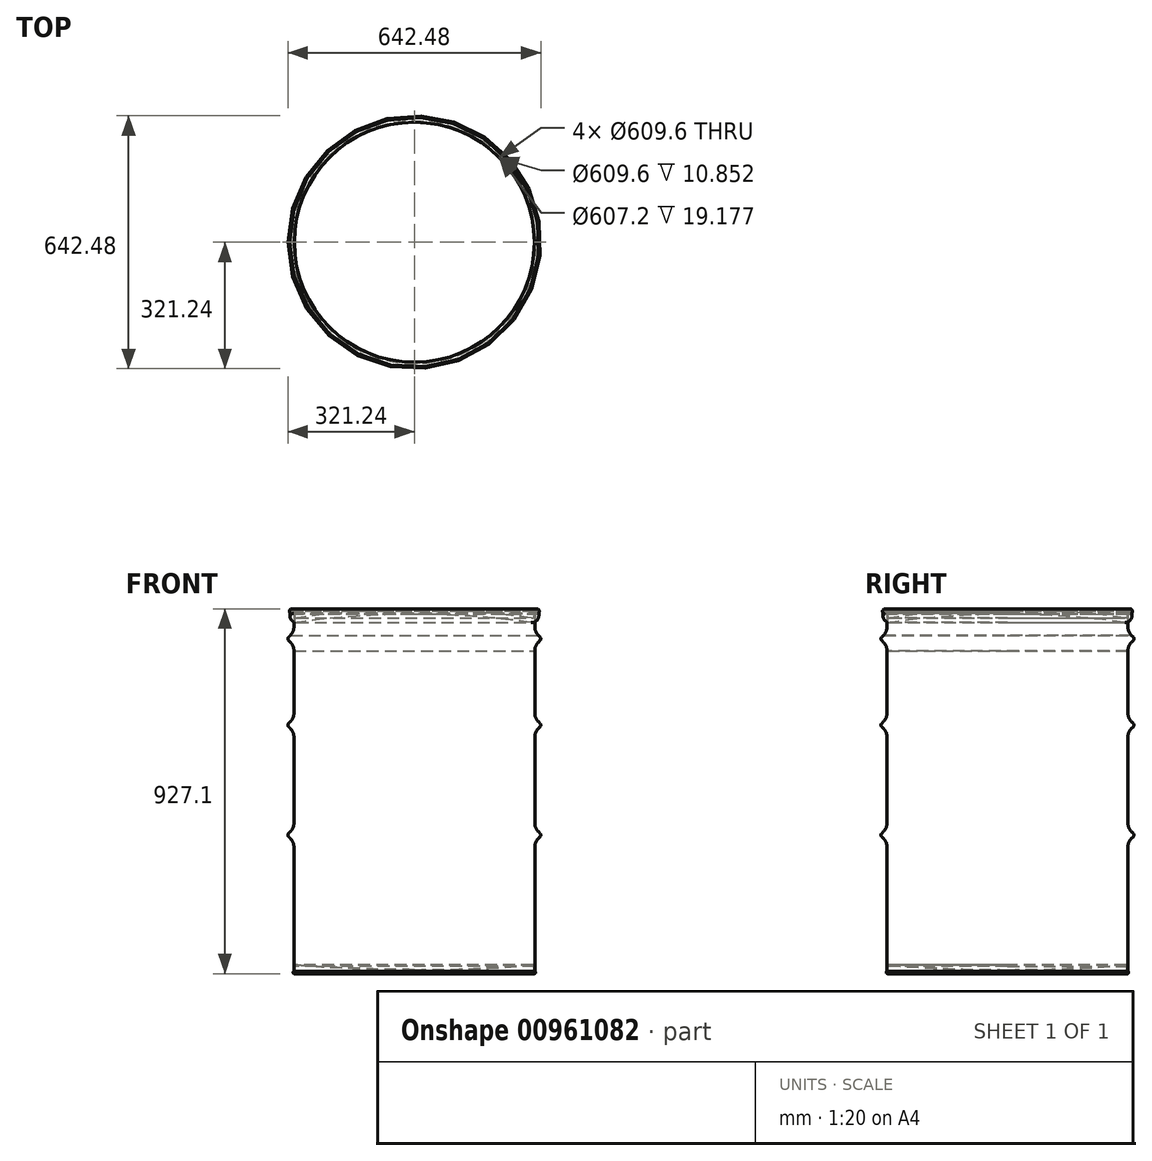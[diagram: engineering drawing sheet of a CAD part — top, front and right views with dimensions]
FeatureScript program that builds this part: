
annotation { "Feature Type Name" : "Feature", "Feature Type Description" : "" }
export const myFeature = defineFeature(function(context is Context, id is Id, definition is map)
    precondition{}
    {
        {
            var Q0;
            Q0=qCreatedBy(makeId("Front.planeOp"),FACE);
            var sketch = newSketch(context, id + "F0", { "sketchPlane" : qUnion([Q0])});
            skLineSegment(sketch, "E0.top", {"start": v(-306, 920.75) * mm, "end": v(-304.8, 920.75) * mm, "construction": true});
            skLineSegment(sketch, "E0.right", {"start": v(-304.8, 0) * mm, "end": v(-304.8, 321.86) * mm});
            skLineSegment(sketch, "E1", {"start": v(0, 0) * mm, "end": v(0, 177.34) * mm, "construction": true});
            skArc(sketch, "E2", {"start": v(-304.8, 920.75) * mm, "mid": v(-316.84, 923.57) * mm, "end": v(-307.3, 915.7) * mm});
            skArc(sketch, "E3", {"start": v(-306, 920.75) * mm, "mid": v(-315.77, 923.04) * mm, "end": v(-308.03, 916.65) * mm});
            skLineSegment(sketch, "E4", {"start": v(-308.03, 916.65) * mm, "end": v(-307.3, 915.7) * mm});
            skArc(sketch, "E5", {"start": v(-304.8, 0) * mm, "mid": v(-307.92, 2.56) * mm, "end": v(-306, 6.11) * mm});
            skLineSegment(sketch, "E6.trimOffspring", {"start": v(-306, 6.11) * mm, "end": v(-306, 321.86) * mm});
            skPoint(sketch, "E0.left.start.orphan", {"position": v(-306, 0) * mm});
            skLineSegment(sketch, "E7", {"start": v(-314.89, 859.88) * mm, "end": v(-319.38, 855.4) * mm});
            skLineSegment(sketch, "E8", {"start": v(-319.38, 846.4) * mm, "end": v(-314.89, 841.92) * mm});
            skLineSegment(sketch, "E9.trimOffspring", {"start": v(-306, 881.34) * mm, "end": v(-306, 920.75) * mm});
            skArc(sketch, "E10.filletArc", {"start": v(-319.38, 855.4) * mm, "mid": v(-321.24, 850.9) * mm, "end": v(-319.38, 846.4) * mm});
            skArc(sketch, "E11.filletArc", {"start": v(-314.89, 859.88) * mm, "mid": v(-308.31, 869.73) * mm, "end": v(-306, 881.34) * mm});
            skArc(sketch, "E12.filletArc", {"start": v(-306, 820.46) * mm, "mid": v(-308.31, 832.07) * mm, "end": v(-314.89, 841.92) * mm});
            skLineSegment(sketch, "E13", {"start": v(-321.24, 805.66) * mm, "end": v(-321.24, 227.24) * mm, "construction": true});
            skLineSegment(sketch, "E14", {"start": v(-311.15, 920.75) * mm, "end": v(-311.15, 927.1) * mm, "construction": true});
            skLineSegment(sketch, "E15", {"start": v(-319.38, 855.4) * mm, "end": v(-319.38, 846.4) * mm, "construction": true});
            skLineSegment(sketch, "E16", {"start": v(-314.89, 859.88) * mm, "end": v(-314.89, 841.92) * mm, "construction": true});
            skLineSegment(sketch, "E17", {"start": v(-306, 820.46) * mm, "end": v(-304.8, 820.46) * mm, "construction": true});
            skLineSegment(sketch, "E18", {"start": v(-306, 881.34) * mm, "end": v(-304.8, 881.34) * mm, "construction": true});
            skLineSegment(sketch, "E19.trimOffspring", {"start": v(-304.8, 881.34) * mm, "end": v(-304.8, 920.75) * mm});
            skLineSegment(sketch, "E20", {"start": v(-318.4, 847.39) * mm, "end": v(-313.91, 842.9) * mm});
            skLineSegment(sketch, "E21", {"start": v(-318.4, 854.41) * mm, "end": v(-313.91, 858.9) * mm});
            skArc(sketch, "E22", {"start": v(-318.4, 854.41) * mm, "mid": v(-319.86, 850.9) * mm, "end": v(-318.4, 847.39) * mm});
            skArc(sketch, "E23", {"start": v(-313.91, 858.9) * mm, "mid": v(-307.17, 869.23) * mm, "end": v(-304.8, 881.34) * mm});
            skArc(sketch, "E24", {"start": v(-304.8, 820.46) * mm, "mid": v(-307.08, 832.6) * mm, "end": v(-313.91, 842.9) * mm});
            skLineSegment(sketch, "E25", {"start": v(-314.89, 640.68) * mm, "end": v(-319.38, 636.19) * mm});
            skLineSegment(sketch, "E26", {"start": v(-319.38, 627.2) * mm, "end": v(-314.89, 622.72) * mm});
            skLineSegment(sketch, "E27.trimOffspring", {"start": v(-306, 662.14) * mm, "end": v(-306, 820.46) * mm});
            skPoint(sketch, "E28.visualSharp", {"position": v(-323.87, 631.7) * mm});
            skArc(sketch, "E28.filletArc", {"start": v(-319.38, 636.19) * mm, "mid": v(-321.24, 631.7) * mm, "end": v(-319.38, 627.2) * mm});
            skArc(sketch, "E29.filletArc", {"start": v(-314.89, 640.68) * mm, "mid": v(-308.31, 650.53) * mm, "end": v(-306, 662.14) * mm});
            skArc(sketch, "E30.filletArc", {"start": v(-306, 601.26) * mm, "mid": v(-308.31, 612.87) * mm, "end": v(-314.89, 622.72) * mm});
            skLineSegment(sketch, "E31", {"start": v(-314.89, 640.68) * mm, "end": v(-314.89, 622.72) * mm, "construction": true});
            skLineSegment(sketch, "E32", {"start": v(-306, 601.26) * mm, "end": v(-304.8, 601.26) * mm, "construction": true});
            skLineSegment(sketch, "E33", {"start": v(-306, 662.14) * mm, "end": v(-304.8, 662.14) * mm, "construction": true});
            skLineSegment(sketch, "E34.trimOffspring", {"start": v(-304.8, 662.14) * mm, "end": v(-304.8, 820.46) * mm});
            skLineSegment(sketch, "E35", {"start": v(-318.53, 635.34) * mm, "end": v(-314.04, 639.83) * mm});
            skArc(sketch, "E36", {"start": v(-314.04, 639.83) * mm, "mid": v(-307.2, 650.07) * mm, "end": v(-304.8, 662.14) * mm});
            skLineSegment(sketch, "E37", {"start": v(-318.53, 628.06) * mm, "end": v(-314.04, 623.57) * mm});
            skArc(sketch, "E38", {"start": v(-304.8, 601.26) * mm, "mid": v(-307.2, 613.33) * mm, "end": v(-314.04, 623.57) * mm});
            skArc(sketch, "E39", {"start": v(-318.53, 635.34) * mm, "mid": v(-320.04, 631.7) * mm, "end": v(-318.53, 628.06) * mm});
            skLineSegment(sketch, "E40", {"start": v(-314.89, 361.28) * mm, "end": v(-319.38, 356.79) * mm});
            skLineSegment(sketch, "E41", {"start": v(-319.38, 347.8) * mm, "end": v(-314.9, 343.32) * mm});
            skArc(sketch, "E42.filletArc", {"start": v(-319.38, 356.79) * mm, "mid": v(-321.24, 352.3) * mm, "end": v(-319.38, 347.8) * mm});
            skLineSegment(sketch, "E43.trimOffspring", {"start": v(-306, 382.74) * mm, "end": v(-306, 601.26) * mm});
            skArc(sketch, "E44.filletArc", {"start": v(-314.9, 361.28) * mm, "mid": v(-308.31, 371.13) * mm, "end": v(-306, 382.74) * mm});
            skArc(sketch, "E45.filletArc", {"start": v(-306, 321.86) * mm, "mid": v(-308.31, 333.47) * mm, "end": v(-314.89, 343.32) * mm});
            skLineSegment(sketch, "E46", {"start": v(-319.38, 356.79) * mm, "end": v(-319.38, 347.8) * mm, "construction": true});
            skLineSegment(sketch, "E47", {"start": v(-314.89, 361.28) * mm, "end": v(-314.89, 343.32) * mm, "construction": true});
            skLineSegment(sketch, "E48", {"start": v(-306, 382.74) * mm, "end": v(-304.8, 382.74) * mm, "construction": true});
            skLineSegment(sketch, "E49", {"start": v(-306, 321.86) * mm, "end": v(-304.8, 321.86) * mm, "construction": true});
            skLineSegment(sketch, "E50.trimOffspring", {"start": v(-304.8, 382.74) * mm, "end": v(-304.8, 601.26) * mm});
            skLineSegment(sketch, "E51", {"start": v(-318.53, 355.94) * mm, "end": v(-314.04, 360.43) * mm});
            skLineSegment(sketch, "E52", {"start": v(-318.53, 348.66) * mm, "end": v(-314.04, 344.17) * mm});
            skArc(sketch, "E53", {"start": v(-314.04, 360.43) * mm, "mid": v(-307.2, 370.67) * mm, "end": v(-304.8, 382.74) * mm});
            skArc(sketch, "E54", {"start": v(-304.8, 321.86) * mm, "mid": v(-307.2, 333.93) * mm, "end": v(-314.04, 344.17) * mm});
            skArc(sketch, "E55", {"start": v(-318.53, 355.94) * mm, "mid": v(-320.04, 352.3) * mm, "end": v(-318.53, 348.66) * mm});
            skSolve(sketch);
        }
        {
            var Q0;
            Q0=qSketchRegion(id+"F0",true);
            var Q1;
            Q1=qConstructionFilter(qBodyType(qCreatedBy(id+"F0",EDGE),BodyType.WIRE),ConstructionObject.NO);
            var Q2;
            Q2=sQuery(id+"F0.wireOp",EDGE,"E1");
            revolve(context, id + "F1", {"entities" : qUnion([Q0]), "surfaceEntities" : qUnion([Q1]), "axis" : qUnion([Q2]), "revolveType" : RevolveType.FULL});
        }
        {
            var Q0;
            Q0=qCreatedBy(makeId("Front.planeOp"),FACE);
            var sketch = newSketch(context, id + "F2", { "sketchPlane" : qUnion([Q0])});
            skLineSegment(sketch, "E56", {"start": v(306, 6.11) * mm, "end": v(306, 321.86) * mm});
            skArc(sketch, "E57", {"start": v(304.8, 0) * mm, "mid": v(307.92, 2.56) * mm, "end": v(306, 6.11) * mm});
            skLineSegment(sketch, "E58", {"start": v(304.8, 0) * mm, "end": v(304.8, 321.86) * mm});
            skLineSegment(sketch, "E59", {"start": v(-304.8, 321.86) * mm, "end": v(-304.8, 0) * mm});
            skLineSegment(sketch, "E60", {"start": v(-304.8, 0) * mm, "end": v(-303.6, 0) * mm});
            skLineSegment(sketch, "E61", {"start": v(-303.6, 0) * mm, "end": v(-303.6, 19.18) * mm});
            skArc(sketch, "E62", {"start": v(-301.47, 21.15) * mm, "mid": v(-302.96, 20.63) * mm, "end": v(-303.6, 19.18) * mm});
            skLineSegment(sketch, "E63", {"start": v(0, 244.83) * mm, "end": v(0, -50.53) * mm, "construction": true});
            skArc(sketch, "E64", {"start": v(-301.47, 21.15) * mm, "mid": v(-150.85, 12.15) * mm, "end": v(0, 9.14) * mm});
            skLineSegment(sketch, "E65", {"start": v(0, 9.14) * mm, "end": v(0, 10.34) * mm});
            skArc(sketch, "E66", {"start": v(-304.8, 19.18) * mm, "mid": v(-303.78, 21.5) * mm, "end": v(-301.37, 22.34) * mm});
            skArc(sketch, "E67", {"start": v(-301.37, 22.34) * mm, "mid": v(-150.8, 13.34) * mm, "end": v(0, 10.34) * mm});
            skLineSegment(sketch, "E68", {"start": v(-301.63, 19.18) * mm, "end": v(-301.63, 22.35) * mm, "construction": true});
            skSolve(sketch);
        }
        {
            var Q0;
            Q0=qSketchRegion(id+"F2",true);
            var Q1;
            Q1=sQuery(id+"F2.wireOp",EDGE,"E63");
            revolve(context, id + "F3", {"operationType" : NewBodyOperationType.ADD, "entities" : qUnion([Q0]), "axis" : qUnion([Q1]), "revolveType" : RevolveType.FULL});
        }
        {
            var Q0;
            Q0=qCreatedBy(makeId("Front.planeOp"),FACE);
            var sketch = newSketch(context, id + "F4", { "sketchPlane" : qUnion([Q0])});
            skLineSegment(sketch, "E69", {"start": v(0, 998.16) * mm, "end": v(0, -198.69) * mm, "construction": true});
            skArc(sketch, "E70", {"start": v(-307.3, 915.7) * mm, "mid": v(-316.84, 923.57) * mm, "end": v(-304.8, 920.75) * mm, "construction": true});
            skLineSegment(sketch, "E71", {"start": v(-304.8, 920.75) * mm, "end": v(-304.8, 881.34) * mm, "construction": true});
            skLineSegment(sketch, "E72", {"start": v(-304.8, 920.75) * mm, "end": v(-304.8, 920.75) * mm});
            skLineSegment(sketch, "E73", {"start": v(-304.8, 920.75) * mm, "end": v(-304.8, 909.9) * mm});
            skArc(sketch, "E74", {"start": v(-304.8, 909.9) * mm, "mid": v(-302.61, 905.1) * mm, "end": v(-297.55, 903.61) * mm});
            skArc(sketch, "E75", {"start": v(-297.55, 903.61) * mm, "mid": v(-149.15, 919.42) * mm, "end": v(0, 924.7) * mm});
            skLineSegment(sketch, "E76", {"start": v(-304.8, 920.75) * mm, "end": v(-306, 920.75) * mm});
            skArc(sketch, "E77", {"start": v(-306, 920.75) * mm, "mid": v(-311.15, 915.6) * mm, "end": v(-316.3, 920.75) * mm});
            skLineSegment(sketch, "E78", {"start": v(-316.3, 920.75) * mm, "end": v(-316.3, 909.9) * mm});
            skArc(sketch, "E79", {"start": v(-316.3, 909.9) * mm, "mid": v(-310.15, 896.42) * mm, "end": v(-295.93, 892.23) * mm});
            skArc(sketch, "E80", {"start": v(-295.93, 892.23) * mm, "mid": v(-148.34, 907.95) * mm, "end": v(0, 913.2) * mm});
            skLineSegment(sketch, "E81", {"start": v(0, 924.7) * mm, "end": v(0, 913.2) * mm});
            skLineSegment(sketch, "E82", {"start": v(-298.45, 909.9) * mm, "end": v(-297.55, 903.61) * mm, "construction": true});
            skLineSegment(sketch, "E83", {"start": v(-298.45, 909.9) * mm, "end": v(-298.45, 903.55) * mm, "construction": true});
            skLineSegment(sketch, "E84", {"start": v(-311.15, 920.75) * mm, "end": v(-311.15, 925.9) * mm, "construction": true});
            skSolve(sketch);
        }
        {
            var Q0;
            Q0=qSketchRegion(id+"F4",true);
            var Q1;
            Q1=sQuery(id+"F4.wireOp",EDGE,"E69");
            revolve(context, id + "F5", {"entities" : qUnion([Q0]), "axis" : qUnion([Q1]), "revolveType" : RevolveType.FULL});
        }
    });
